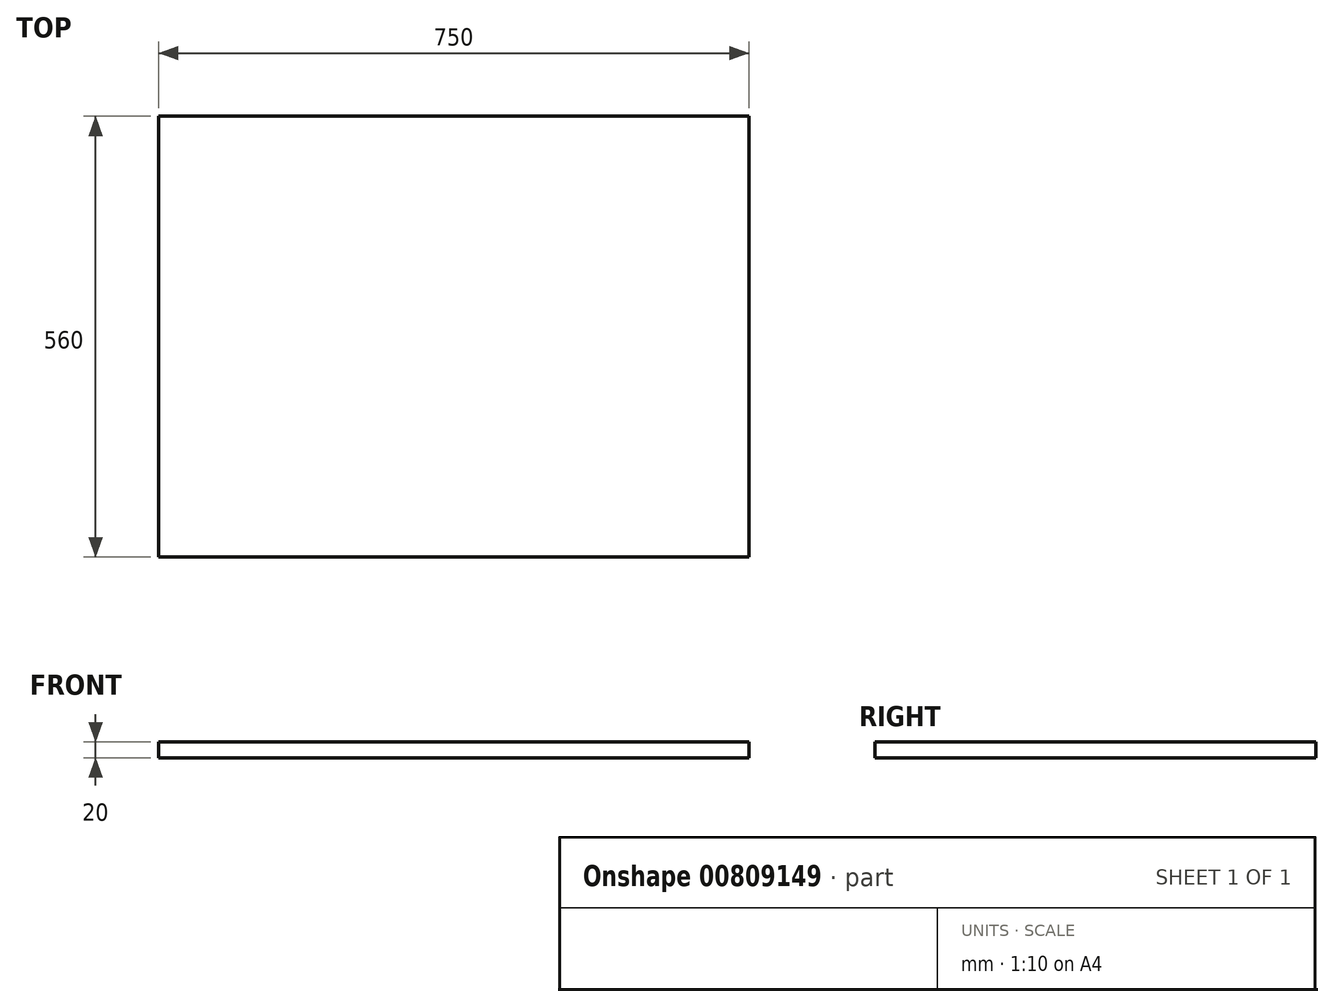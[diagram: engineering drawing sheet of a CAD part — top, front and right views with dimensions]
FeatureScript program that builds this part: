
annotation { "Feature Type Name" : "Feature", "Feature Type Description" : "" }
export const myFeature = defineFeature(function(context is Context, id is Id, definition is map)
    precondition{}
    {
        {
            var Q0;
            Q0=qCreatedBy(makeId("Top.planeOp"),FACE);
            var sketch = newSketch(context, id + "F0", { "sketchPlane" : qUnion([Q0])});
            skLineSegment(sketch, "E0.bottom", {"start": v(375, -280) * mm, "end": v(-375, -280) * mm});
            skLineSegment(sketch, "E0.top", {"start": v(375, 280) * mm, "end": v(-375, 280) * mm});
            skLineSegment(sketch, "E0.left", {"start": v(375, -280) * mm, "end": v(375, 280) * mm});
            skLineSegment(sketch, "E0.right", {"start": v(-375, -280) * mm, "end": v(-375, 280) * mm});
            skPoint(sketch, "E0.middle", {"position": v(0, 0) * mm});
            skSolve(sketch);
        }
        {
            var Q0;
            Q0=makeQuery(id+"F0.imprint","IMPRINT",FACE,{"disambiguationData":[TD([[makeQuery(id+"F0.imprint","IMPRINT",EDGE,{"derivedFrom":sQuery(id+"F0.wireOp",EDGE,"E0.bottom")}),-1.0]])]});
            extrude(context, id + "F1", {"entities" : qUnion([Q0]), "depth" : 20 * mm, "offsetDistance" : 25 * mm});
        }
    });
